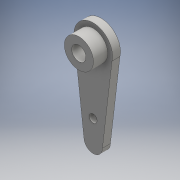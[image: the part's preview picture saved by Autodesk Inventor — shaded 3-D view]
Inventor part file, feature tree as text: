
AUTODESK INVENTOR PART (.ipt)
format: ipt  version: 2016 (Build 200138000, 138)  size: 122,880 bytes
history: native  units: mm
features: sketch x4, extrude x3, hole x1
ambient origin geometry x8: Origin, YZ Plane, XZ Plane, XY Plane, X Axis, Y Axis, Z Axis, Center Point
bodies: Solid1 (feature_tree)
feature tree (8):
  extrude  "Extrusion1"  Depth=5.4mm
  extrude  "Extrusion2"  Depth=5.4mm
  extrude  "Extrusion3"  Depth=3.0mm
  hole  "Hole2"  [1 undecoded]
  sketch  "Sketch1"  dims[d0=5.4mm d1=11.0mm]
  sketch  "Sketch2"  dims[d2=5.4mm d3=0.0mm d4=14.6mm]
  sketch  "Sketch3"  dims[d5=3.0mm d6=0.0mm d7=7.0mm]
  sketch  "Sketch5"  dims[d8=32.0mm d9=3.0mm d10=0.0mm d18=24.0mm d19=3.0mm d20=6.0mm d21=4.0mm d22=2.0mm d23=90.0deg d24=8.0mm d25=20.594885mm]
note: 1 required parameter value undecoded (feature->parameter linkage not recoverable at this tier; creation-order binding heuristic only, values carry confidence <= 0.55)
